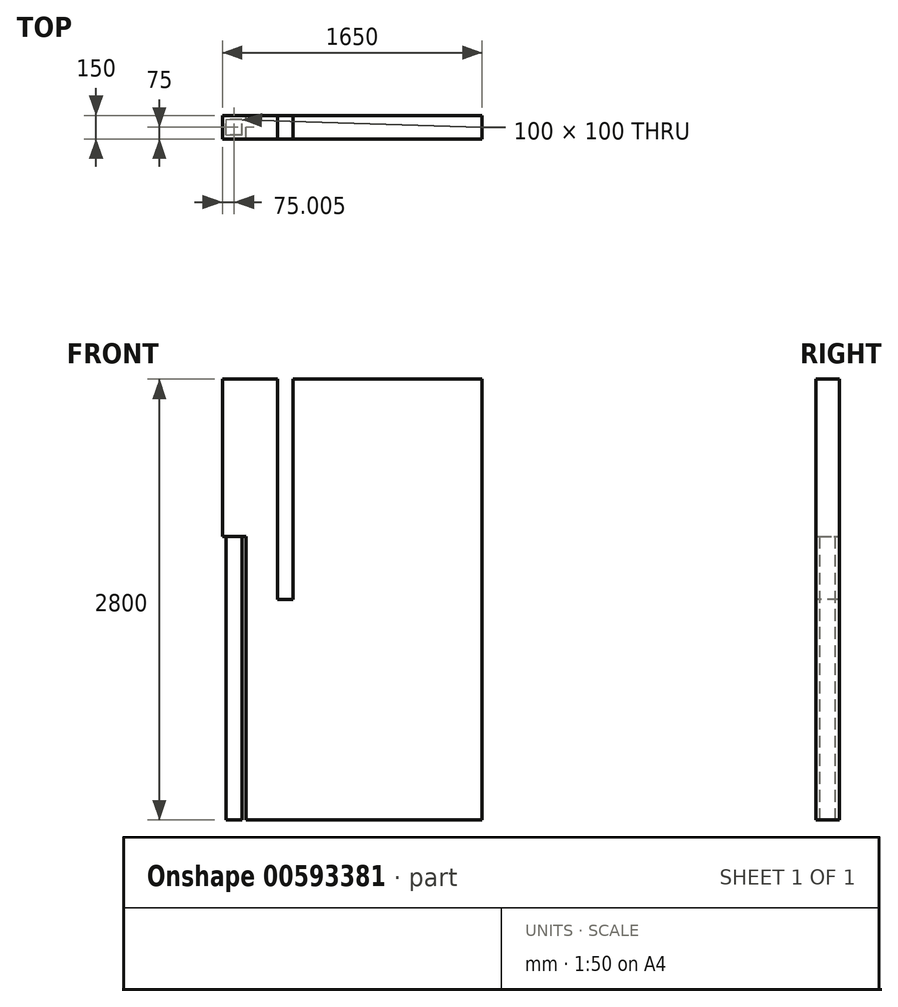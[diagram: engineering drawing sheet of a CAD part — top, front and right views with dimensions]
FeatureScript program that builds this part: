
annotation { "Feature Type Name" : "Feature", "Feature Type Description" : "" }
export const myFeature = defineFeature(function(context is Context, id is Id, definition is map)
    precondition{}
    {
        {
            var Q0;
            Q0=qCreatedBy(makeId("Front.planeOp"),FACE);
            var sketch = newSketch(context, id + "F0", { "sketchPlane" : qUnion([Q0])});
            skLineSegment(sketch, "E0.top", {"start": v(-889.04, -1382.8) * mm, "end": v(610.96, -1382.8) * mm});
            skLineSegment(sketch, "E0.left", {"start": v(-889.04, 417.2) * mm, "end": v(-889.04, -1382.8) * mm});
            skLineSegment(sketch, "E0.right", {"start": v(610.96, 1417.2) * mm, "end": v(610.96, -1382.8) * mm});
            skLineSegment(sketch, "E1.top", {"start": v(-889.04, 417.2) * mm, "end": v(-914.04, 417.2) * mm});
            skLineSegment(sketch, "E1.right", {"start": v(-1039.04, 1417.2) * mm, "end": v(-1039.04, 417.2) * mm});
            skLineSegment(sketch, "E2", {"start": v(-1039.04, 1417.2) * mm, "end": v(610.96, 1417.2) * mm});
            skLineSegment(sketch, "E3.top", {"start": v(-914.04, -1382.8) * mm, "end": v(-1014.04, -1382.8) * mm});
            skLineSegment(sketch, "E3.left", {"start": v(-914.04, 417.2) * mm, "end": v(-914.04, -1382.8) * mm});
            skLineSegment(sketch, "E3.right", {"start": v(-1014.04, 417.2) * mm, "end": v(-1014.04, -1382.8) * mm});
            skLineSegment(sketch, "E4.trimOffspring", {"start": v(-1014.04, 417.2) * mm, "end": v(-1039.04, 417.2) * mm});
            skSolve(sketch);
        }
        {
            var Q0;
            Q0 = qSketchRegion(id + "F0", true);
            extrude(context, id + "F1", {"entities" : qUnion([Q0]), "depth" : 150 * mm, "offsetDistance" : 25 * mm});
        }
        {
            var Q0;
            Q0=makeQuery(id+"F1.opExtrude","SWEPT_FACE",FACE,{"disambiguationData":[OSD([sQuery(id+"F0.wireOp",EDGE,"E3.right")])]});
            var sketch = newSketch(context, id + "F2", { "sketchPlane" : qUnion([Q0])});
            skLineSegment(sketch, "E5.bottom", {"start": v(150, -1382.8) * mm, "end": v(125, -1382.8) * mm});
            skLineSegment(sketch, "E5.top", {"start": v(150, 417.2) * mm, "end": v(125, 417.2) * mm});
            skLineSegment(sketch, "E5.left", {"start": v(150, -1382.8) * mm, "end": v(150, 417.2) * mm});
            skLineSegment(sketch, "E5.right", {"start": v(125, -1382.8) * mm, "end": v(125, 417.2) * mm});
            skLineSegment(sketch, "E6.bottom", {"start": v(0, -1382.8) * mm, "end": v(25, -1382.8) * mm});
            skLineSegment(sketch, "E6.top", {"start": v(0, 417.2) * mm, "end": v(25, 417.2) * mm});
            skLineSegment(sketch, "E6.left", {"start": v(0, -1382.8) * mm, "end": v(0, 417.2) * mm});
            skLineSegment(sketch, "E6.right", {"start": v(25, -1382.8) * mm, "end": v(25, 417.2) * mm});
            skSolve(sketch);
        }
        {
            var Q0;
            Q0 = qSketchRegion(id + "F2", true);
            extrude(context, id + "F3", {"entities" : qUnion([Q0]), "operationType" : NewBodyOperationType.REMOVE, "endBound" : BoundingType.UP_TO_NEXT, "oppositeDirection" : true, "depth" : 25 * mm, "offsetDistance" : 25 * mm});
        }
        {
            var Q0;
            Q0=makeQuery(id+"F1.opExtrude","CAP_FACE",FACE,{"disambiguationData":[OSD([sQuery(id+"F0.wireOp",EDGE,"E0.top"),sQuery(id+"F0.wireOp",EDGE,"E0.left"),sQuery(id+"F0.wireOp",EDGE,"E0.right"),sQuery(id+"F0.wireOp",EDGE,"E1.top"),sQuery(id+"F0.wireOp",EDGE,"E1.right"),sQuery(id+"F0.wireOp",EDGE,"E2"),sQuery(id+"F0.wireOp",EDGE,"E3.top"),sQuery(id+"F0.wireOp",EDGE,"E3.left"),sQuery(id+"F0.wireOp",EDGE,"E3.right"),sQuery(id+"F0.wireOp",EDGE,"E4.trimOffspring")])],"isStart":false});
            var sketch = newSketch(context, id + "F4", { "sketchPlane" : qUnion([Q0])});
            skLineSegment(sketch, "E7.bottom", {"start": v(-689.04, 1417.2) * mm, "end": v(-589.04, 1417.2) * mm});
            skLineSegment(sketch, "E7.top", {"start": v(-689.04, 17.2) * mm, "end": v(-589.04, 17.2) * mm});
            skLineSegment(sketch, "E7.left", {"start": v(-689.04, 1417.2) * mm, "end": v(-689.04, 17.2) * mm});
            skLineSegment(sketch, "E7.right", {"start": v(-589.04, 1417.2) * mm, "end": v(-589.04, 17.2) * mm});
            skSolve(sketch);
        }
        {
            var Q0;
            Q0 = qSketchRegion(id + "F4", true);
            extrude(context, id + "F5", {"entities" : qUnion([Q0]), "operationType" : NewBodyOperationType.REMOVE, "endBound" : BoundingType.UP_TO_NEXT, "oppositeDirection" : true, "depth" : 25 * mm, "offsetDistance" : 25 * mm});
        }
    });
